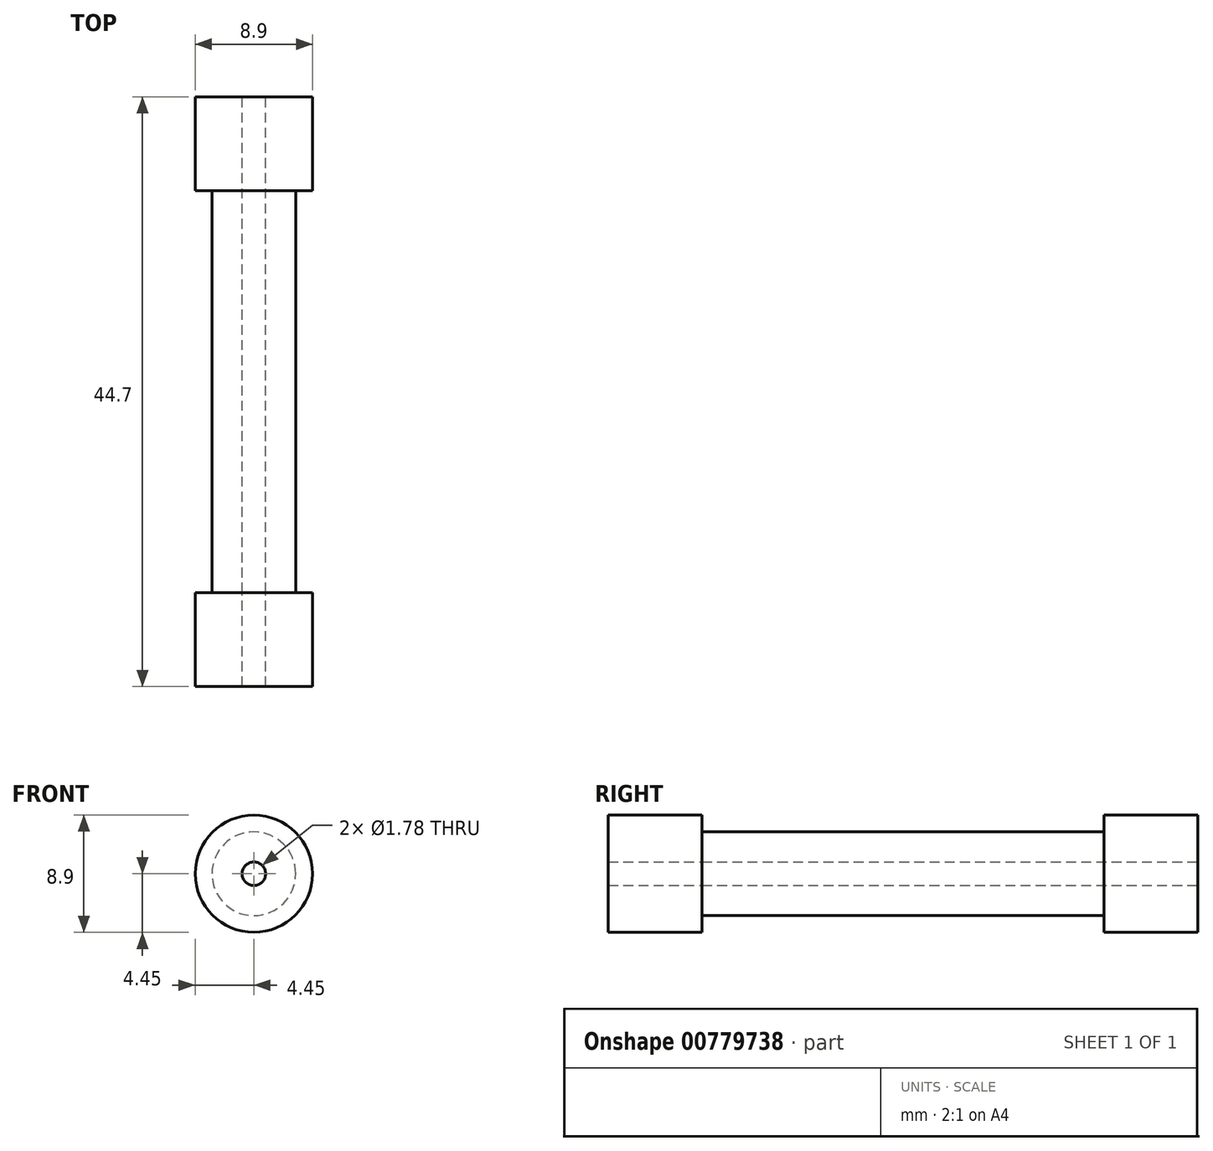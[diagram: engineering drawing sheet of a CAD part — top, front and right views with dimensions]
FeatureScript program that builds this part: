
annotation { "Feature Type Name" : "Feature", "Feature Type Description" : "" }
export const myFeature = defineFeature(function(context is Context, id is Id, definition is map)
    precondition{}
    {
        {
            var Q0;
            Q0=qCreatedBy(makeId("Front.planeOp"),FACE);
            var sketch = newSketch(context, id + "F0", { "sketchPlane" : qUnion([Q0])});
            skCircle(sketch, "E0", {"center": v(0, 0) * mm, "radius": 3.18 * mm});
            skSolve(sketch);
        }
        {
            var Q0;
            Q0 = qSketchRegion(id + "F0", true);
            extrude(context, id + "F1", {"entities" : qUnion([Q0]), "depth" : 30.48 * mm, "offsetDistance" : 25.4 * mm});
        }
        {
            var Q0;
            Q0=makeQuery(id+"F1.opExtrude","CAP_FACE",FACE,{"disambiguationData":[OSD([sQuery(id+"F0.wireOp",EDGE,"E0")])],"isStart":true});
            var sketch = newSketch(context, id + "F2", { "sketchPlane" : qUnion([Q0])});
            skSolve(sketch);
        }
        {
            var Q0;
            Q0=makeQuery(id+"F1.opExtrude","CAP_FACE",FACE,{"disambiguationData":[OSD([sQuery(id+"F0.wireOp",EDGE,"E0")])],"isStart":false});
            var sketch = newSketch(context, id + "F3", { "sketchPlane" : qUnion([Q0])});
            skCircle(sketch, "E1", {"center": v(0, 0) * mm, "radius": 4.45 * mm});
            skSolve(sketch);
        }
        {
            var Q0;
            Q0=makeQuery(id+"F3.imprint","IMPRINT",FACE,{"disambiguationData":[TD([[makeQuery(id+"F3.imprint","IMPRINT",EDGE,{"derivedFrom":makeQuery(id+"F1.opExtrude","CAP_EDGE",EDGE,{"disambiguationData":[OSD([sQuery(id+"F0.wireOp",EDGE,"E0")])],"isStart":false})}),1.0]])]});
            var Q1;
            Q1=makeQuery(id+"F3.imprint","IMPRINT",FACE,{"disambiguationData":[TD([[makeQuery(id+"F3.imprint","IMPRINT",EDGE,{"derivedFrom":sQuery(id+"F3.wireOp",EDGE,"E1")}),1.0]])]});
            extrude(context, id + "F4", {"entities" : qUnion([Q0, Q1]), "depth" : 7.11 * mm, "offsetDistance" : 25.4 * mm});
        }
        {
            var Q0;
            Q0=makeQuery(id+"F2.imprint","IMPRINT",FACE,{"disambiguationData":[TD([[makeQuery(id+"F2.imprint","IMPRINT",EDGE,{"derivedFrom":makeQuery(id+"F1.opExtrude","CAP_EDGE",EDGE,{"disambiguationData":[OSD([sQuery(id+"F0.wireOp",EDGE,"E0")])],"isStart":true})}),-1.0]])]});
            var sketch = newSketch(context, id + "F5", { "sketchPlane" : qUnion([Q0])});
            skCircle(sketch, "E2", {"center": v(0, 0) * mm, "radius": 4.45 * mm});
            skSolve(sketch);
        }
        {
            var Q0;
            Q0=makeQuery(id+"F2.imprint","IMPRINT",FACE,{"disambiguationData":[TD([[makeQuery(id+"F2.imprint","IMPRINT",EDGE,{"derivedFrom":makeQuery(id+"F1.opExtrude","CAP_EDGE",EDGE,{"disambiguationData":[OSD([sQuery(id+"F0.wireOp",EDGE,"E0")])],"isStart":true})}),-1.0]])]});
            var Q1;
            Q1=makeQuery(id+"F5.imprint","IMPRINT",FACE,{"disambiguationData":[TD([[makeQuery(id+"F5.imprint","IMPRINT",EDGE,{"derivedFrom":sQuery(id+"F5.wireOp",EDGE,"E2")}),1.0]])]});
            extrude(context, id + "F6", {"entities" : qUnion([Q0, Q1]), "operationType" : NewBodyOperationType.ADD, "depth" : 7.11 * mm, "offsetDistance" : 25.4 * mm});
        }
        {
            var Q0;
            {var subQ0=sQuery(id+"F0.wireOp",EDGE,"E0");Q0=makeQuery(id+"F6.boolean.opBoolean","MERGE",FACE,{"derivedFrom":[makeQuery(id+"F6.opExtrude","CAP_FACE",FACE,{"disambiguationData":[OSD([subQ0])],"isStart":false}),makeQuery(id+"F6.opExtrude","CAP_FACE",FACE,{"disambiguationData":[OSD([subQ0,sQuery(id+"F5.wireOp",EDGE,"E2")])],"isStart":false})]});}
            var sketch = newSketch(context, id + "F7", { "sketchPlane" : qUnion([Q0])});
            skCircle(sketch, "E3", {"center": v(0, 0) * mm, "radius": 0.89 * mm});
            skSolve(sketch);
        }
        {
            var Q0;
            Q0=makeQuery(id+"F7.imprint","IMPRINT",FACE,{"disambiguationData":[TD([[makeQuery(id+"F7.imprint","IMPRINT",EDGE,{"derivedFrom":sQuery(id+"F7.wireOp",EDGE,"E3")}),1.0]])]});
            extrude(context, id + "F8", {"entities" : qUnion([Q0]), "operationType" : NewBodyOperationType.REMOVE, "oppositeDirection" : true, "depth" : 66.3 * mm, "offsetDistance" : 25.4 * mm});
        }
    });
